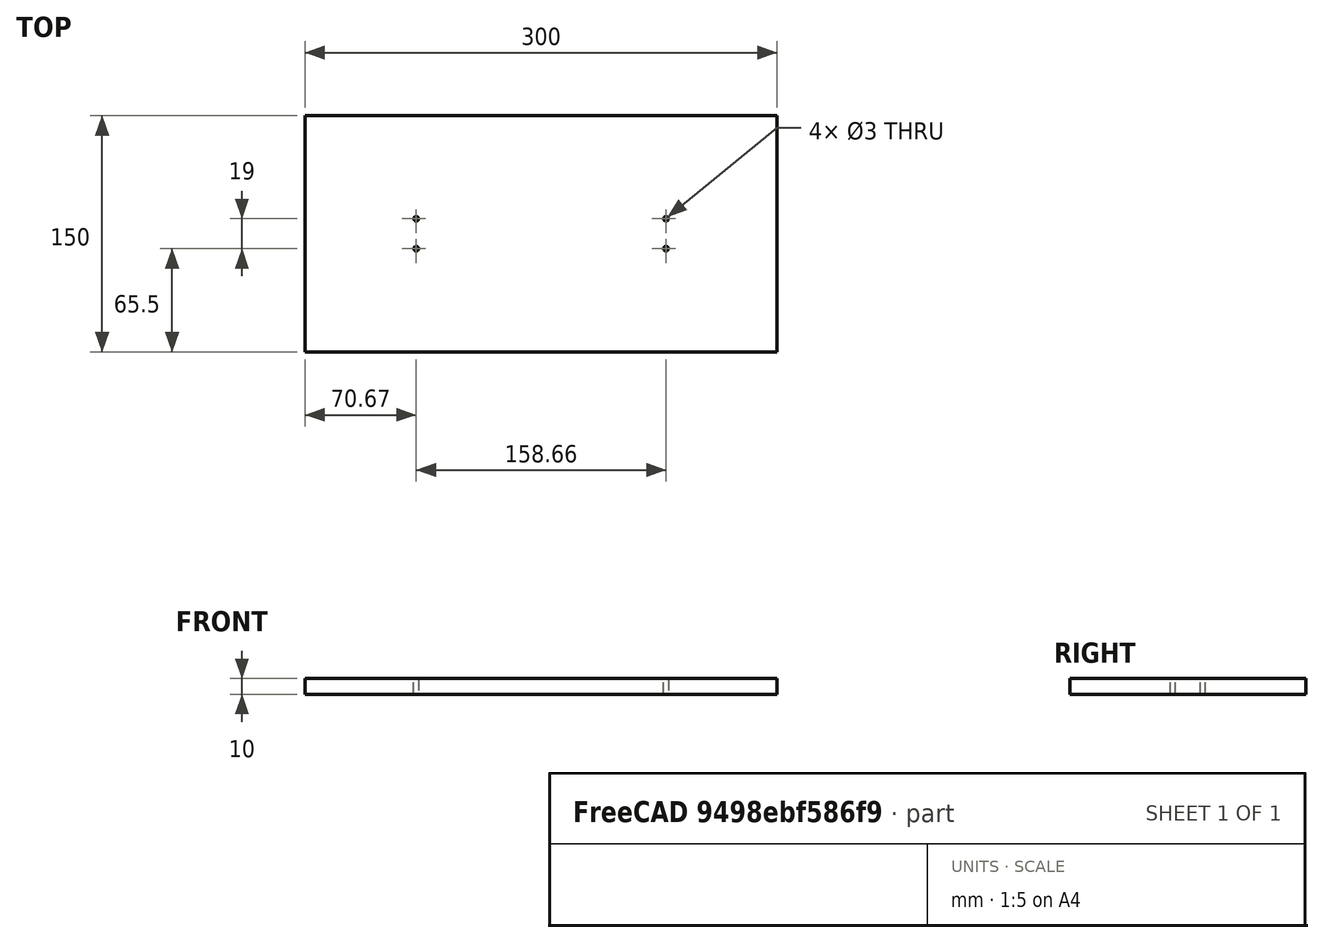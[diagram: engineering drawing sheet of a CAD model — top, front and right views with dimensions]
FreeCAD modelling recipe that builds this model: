
FCSTD DOCUMENT  (FreeCAD 0.19R24267 +99 (Git))
Label: Grundplatte
License: All rights reserved
LicenseURL: http://en.wikipedia.org/wiki/All_rights_reserved
objects: TechDraw::DrawViewDimension×7, Sketcher::SketchObject×2, TechDraw::DrawProjGroupItem×2, PartDesign::Pad×1, PartDesign::Pocket×1, PartDesign::Body×1, TechDraw::DrawSVGTemplate×1, TechDraw::DrawProjGroup×1, TechDraw::DrawPage×1
note: 7 computed .brp shape members not serialized (recipe doc carries the construction recipe); baked Part::Feature solids carry a one-line shape summary decoded from their .brp

FEATURE [Sketcher::SketchObject] Sketch
  FullyConstrained = true
  MapMode = 5
  Support = -> [XY_Plane]
  sketch-geometry (4):
    g0: LineSegment StartX=-150 StartY=75 StartZ=0 EndX=150 EndY=75 EndZ=0
    g1: LineSegment StartX=150 StartY=75 StartZ=0 EndX=150 EndY=-75 EndZ=0
    g2: LineSegment StartX=150 StartY=-75 StartZ=0 EndX=-150 EndY=-75 EndZ=0
    g3: LineSegment StartX=-150 StartY=-75 StartZ=0 EndX=-150 EndY=75 EndZ=0
  constraints (11):
    c: Coincident(g0,g1)
    c: Coincident(g1,g2)
    c: Coincident(g2,g3)
    c: Coincident(g3,g0)
    c: Horizontal(g0)
    c: Horizontal(g2)
    c: Vertical(g1)
    c: Vertical(g3)
    c: Symmetric(g0,g1,g-1)
    c: DistanceX(g0,g0) = 300
    c: DistanceY(g1,g1) = 150
FEATURE [PartDesign::Pad] Pad
  Direction = (1,1,1)
  Length = 10
  Length2 = 100
  Profile = -> Sketch
  Reversed = true
  Type = 0
FEATURE [Sketcher::SketchObject] Sketch001
  ExternalGeometry = -> [Pad]
  FullyConstrained = true
  MapMode = 5
  Support = -> [Pad]
  sketch-geometry (8):
    g0: LineSegment StartX=-79.33 StartY=9.5 StartZ=0 EndX=79.33 EndY=9.5 EndZ=0
    g1: LineSegment StartX=79.33 StartY=9.5 StartZ=0 EndX=79.33 EndY=-9.5 EndZ=0
    g2: LineSegment StartX=79.33 StartY=-9.5 StartZ=0 EndX=-79.33 EndY=-9.5 EndZ=0
    g3: LineSegment StartX=-79.33 StartY=-9.5 StartZ=0 EndX=-79.33 EndY=9.5 EndZ=0
    g4: Circle CenterX=79.33 CenterY=9.5 CenterZ=0 NormalX=0 NormalY=0 NormalZ=1 AngleXU=0 Radius=1.5
    g5: Circle CenterX=79.33 CenterY=-9.5 CenterZ=0 NormalX=0 NormalY=0 NormalZ=1 AngleXU=0 Radius=1.5
    g6: Circle CenterX=-79.33 CenterY=-9.5 CenterZ=0 NormalX=0 NormalY=0 NormalZ=1 AngleXU=0 Radius=1.5
    g7: Circle CenterX=-79.33 CenterY=9.5 CenterZ=0 NormalX=0 NormalY=0 NormalZ=1 AngleXU=0 Radius=1.5
  constraints (19):
    c: Coincident(g0,g1)
    c: Coincident(g1,g2)
    c: Coincident(g2,g3)
    c: Coincident(g3,g0)
    c: Horizontal(g0)
    c: Horizontal(g2)
    c: Vertical(g1)
    c: Vertical(g3)
    c: Symmetric(g0,g1,g-1)
    c: DistanceX(g2,g2) = 158.66
    c: DistanceY(g1,g1) = 19
    c: Coincident(g4,g0)
    c: Coincident(g5,g1)
    c: Coincident(g6,g2)
    c: Coincident(g7,g0)
    c: Equal(g7,g6)
    c: Equal(g6,g5)
    c: Equal(g5,g4)
    c: Diameter(g4) = 3
FEATURE [PartDesign::Pocket] Pocket
  BaseFeature = -> Pad
  Length = 100
  Length2 = 100
  Profile = -> Sketch001
  Type = 0
FEATURE [PartDesign::Body] Body
  Group = -> [Sketch,Pad,Sketch001,Pocket]
  Origin = -> Origin
  Tip = -> Pocket
FEATURE [TechDraw::DrawSVGTemplate] Template
  EditableTexts = APPROVER_NAME=Grundplatte; AUTHOR_NAME=Amelie, Jan, Simon; DATE=2022-02-23; DOCUMENT_TYPE=Mechanical assembly drawing; REVISION=REV A; RIGHTS=(R) DO NOT DUPLICATE THIS DRAWING TO THIRD PARTIES WITHOUT OWNER'S PERMISSION!; SCALE=1:1; SHEET=01; SIZE=A3; TITLELINE-1=Grundplatte
  Height = 297
  Orientation = 1
  Width = 420
FEATURE [TechDraw::DrawProjGroupItem] ProjItem  label="Front"
  CoarseView = false
  Direction = (0,-1,0)
  Focus = 100
  HardHidden = false
  IsoCount = 0
  IsoHidden = false
  IsoVisible = false
  LockPosition = true
  Perspective = false
  Rotation = 0
  RotationVector = (1,0,0)
  ScaleType = 2
  SeamHidden = false
  SeamVisible = true
  SmoothHidden = false
  SmoothVisible = true
  Source = -> [Body]
  Type = 0
  X = 0
  XDirection = (1,0,0)
  Y = 0
FEATURE [TechDraw::DrawProjGroupItem] ProjItem001  label="Bottom"
  CoarseView = false
  Direction = (0,0,-1)
  Focus = 100
  HardHidden = false
  IsoCount = 0
  IsoHidden = false
  IsoVisible = false
  LockPosition = false
  Perspective = false
  Rotation = 0
  RotationVector = (1,0,0)
  ScaleType = 2
  SeamHidden = false
  SeamVisible = true
  SmoothHidden = false
  SmoothVisible = false
  Source = -> [Body]
  Type = 5
  X = 0
  XDirection = (1,0,0)
  Y = 125.838
FEATURE [TechDraw::DrawProjGroup] ProjGroup
  Anchor = -> ProjItem
  AutoDistribute = true
  LockPosition = false
  ProjectionType = 0
  Rotation = 0
  ScaleType = 0
  Source = -> [Body]
  Views = -> [ProjItem,ProjItem001]
  X = 195.226
  Y = 73.7746
  spacingX = 15
  spacingY = 15
FEATURE [TechDraw::DrawViewDimension] Dimension
  Arbitrary = false
  ArbitraryTolerances = false
  EqualTolerance = true
  FormatSpec = %.2f
  FormatSpecOverTolerance = %+.2f
  FormatSpecUnderTolerance = %+.2f
  Inverted = false
  LockPosition = false
  MeasureType = 1
  OverTolerance = 0
  References2D = -> [ProjItem001]
  Rotation = 0
  ScaleType = 0
  TheoreticalExact = false
  Type = 1
  UnderTolerance = 0
  X = -2.23606
  Y = -105.746
FEATURE [TechDraw::DrawViewDimension] Dimension001
  Arbitrary = false
  ArbitraryTolerances = false
  EqualTolerance = true
  FormatSpec = %.2f
  FormatSpecOverTolerance = %+.2f
  FormatSpecUnderTolerance = %+.2f
  Inverted = false
  LockPosition = false
  MeasureType = 1
  OverTolerance = 0
  References2D = -> [ProjItem]
  Rotation = 0
  ScaleType = 0
  TheoreticalExact = false
  Type = 2
  UnderTolerance = 0
  X = 163.416
  Y = 1.67705
FEATURE [TechDraw::DrawViewDimension] Dimension002
  Arbitrary = false
  ArbitraryTolerances = false
  EqualTolerance = true
  FormatSpec = %.2f
  FormatSpecOverTolerance = %+.2f
  FormatSpecUnderTolerance = %+.2f
  Inverted = false
  LockPosition = false
  MeasureType = 1
  OverTolerance = 0
  References2D = -> [ProjItem001]
  Rotation = 0
  ScaleType = 0
  TheoreticalExact = false
  Type = 2
  UnderTolerance = 0
  X = 188.572
  Y = -1.58388
FEATURE [TechDraw::DrawViewDimension] Dimension003
  Arbitrary = false
  ArbitraryTolerances = false
  EqualTolerance = true
  FormatSpec = %.2f
  FormatSpecOverTolerance = %+.2f
  FormatSpecUnderTolerance = %+.2f
  Inverted = false
  LockPosition = false
  MeasureType = 1
  OverTolerance = 0
  References2D = -> [ProjItem001]
  Rotation = 0
  ScaleType = 0
  TheoreticalExact = false
  Type = 1
  UnderTolerance = 0
  X = -120.255
  Y = -92.5614
FEATURE [TechDraw::DrawViewDimension] Dimension004
  Arbitrary = false
  ArbitraryTolerances = false
  EqualTolerance = true
  FormatSpec = %.2f
  FormatSpecOverTolerance = %+.2f
  FormatSpecUnderTolerance = %+.2f
  Inverted = false
  LockPosition = false
  MeasureType = 1
  OverTolerance = 0
  References2D = -> [ProjItem001]
  Rotation = 0
  ScaleType = 0
  TheoreticalExact = false
  Type = 1
  UnderTolerance = 0
  X = -3.91311
  Y = -92.2343
FEATURE [TechDraw::DrawViewDimension] Dimension005
  Arbitrary = false
  ArbitraryTolerances = false
  EqualTolerance = true
  FormatSpec = %.2f
  FormatSpecOverTolerance = %+.2f
  FormatSpecUnderTolerance = %+.2f
  Inverted = false
  LockPosition = false
  MeasureType = 1
  OverTolerance = 0
  References2D = -> [ProjItem001]
  Rotation = 0
  ScaleType = 0
  TheoreticalExact = false
  Type = 2
  UnderTolerance = 0
  X = 167.772
  Y = -38.5232
FEATURE [TechDraw::DrawViewDimension] Dimension006
  Arbitrary = false
  ArbitraryTolerances = false
  EqualTolerance = true
  FormatSpec = %.2f
  FormatSpecOverTolerance = %+.2f
  FormatSpecUnderTolerance = %+.2f
  Inverted = false
  LockPosition = false
  MeasureType = 1
  OverTolerance = 0
  References2D = -> [ProjItem001]
  Rotation = 0
  ScaleType = 0
  TheoreticalExact = false
  Type = 2
  UnderTolerance = 0
  X = 167.841
  Y = 1.39754
FEATURE [TechDraw::DrawPage] Page
  KeepUpdated = true
  NextBalloonIndex = 1
  ProjectionType = 0
  Template = -> Template
  Views = -> [ProjGroup,Dimension,Dimension001,Dimension002,Dimension003,Dimension004,Dimension005,Dimension006]
